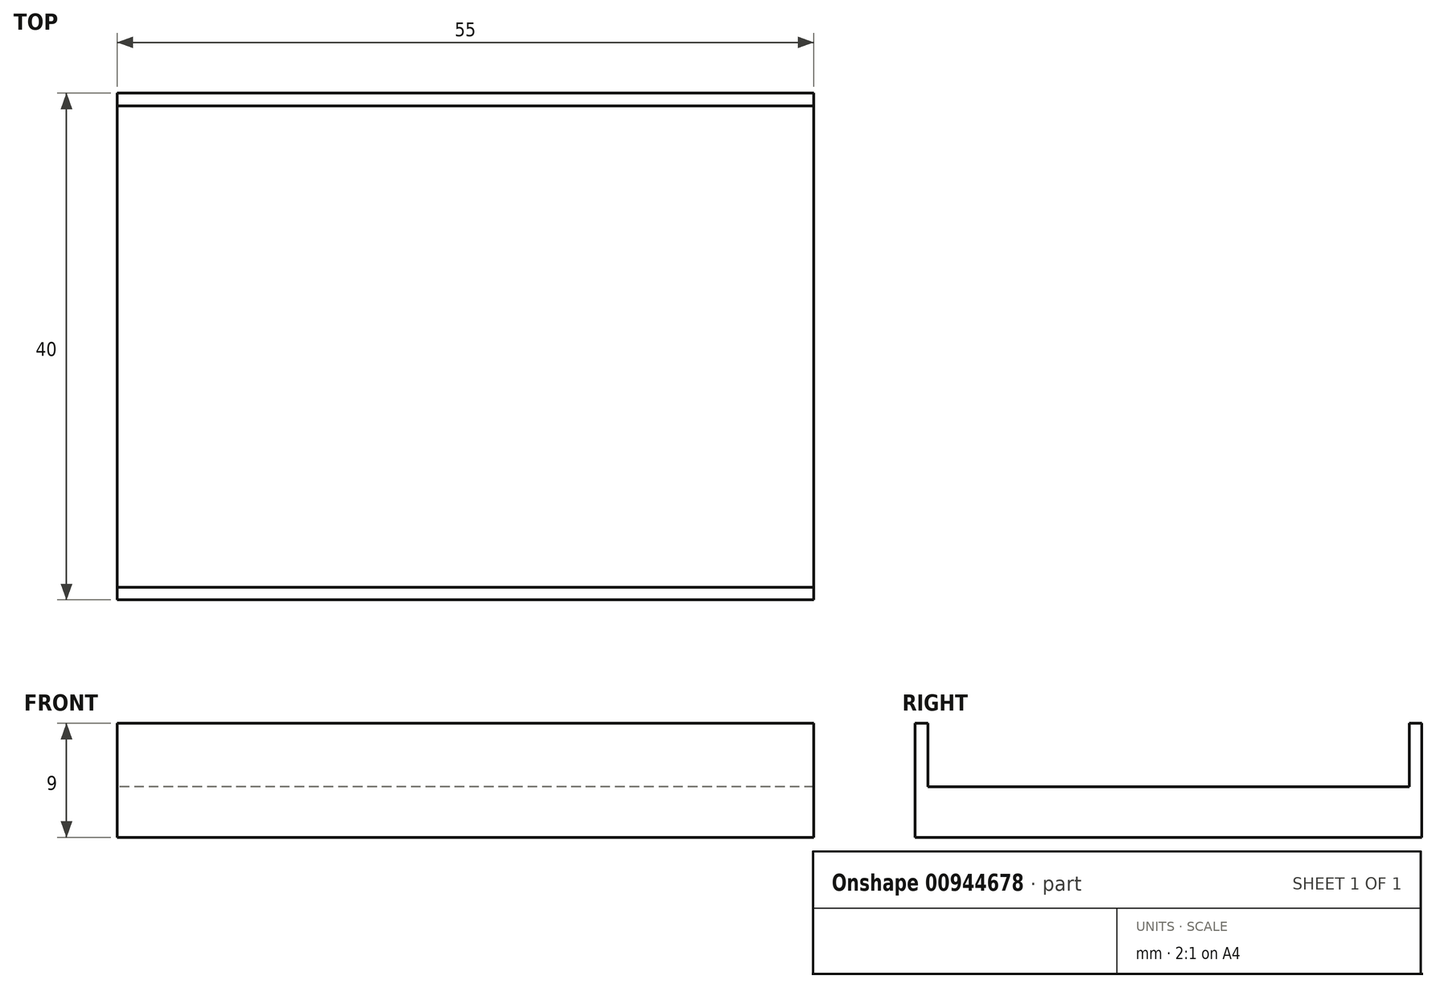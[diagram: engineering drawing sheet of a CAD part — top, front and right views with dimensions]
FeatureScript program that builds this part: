
annotation { "Feature Type Name" : "Feature", "Feature Type Description" : "" }
export const myFeature = defineFeature(function(context is Context, id is Id, definition is map)
    precondition{}
    {
        {
            var Q0;
            Q0=qCreatedBy(makeId("Top.planeOp"),FACE);
            var sketch = newSketch(context, id + "F0", { "sketchPlane" : qUnion([Q0])});
            skLineSegment(sketch, "E0.bottom", {"start": v(27.5, 20) * mm, "end": v(-27.5, 20) * mm});
            skLineSegment(sketch, "E0.top", {"start": v(27.5, -20) * mm, "end": v(-27.5, -20) * mm});
            skLineSegment(sketch, "E0.left", {"start": v(27.5, 20) * mm, "end": v(27.5, -20) * mm});
            skLineSegment(sketch, "E0.right", {"start": v(-27.5, 20) * mm, "end": v(-27.5, -20) * mm});
            skPoint(sketch, "E0.middle", {"position": v(0, 0) * mm});
            skSolve(sketch);
        }
        {
            var Q0;
            Q0=makeQuery(id+"F0.imprint","IMPRINT",FACE,{"disambiguationData":[TD([[makeQuery(id+"F0.imprint","IMPRINT",EDGE,{"derivedFrom":sQuery(id+"F0.wireOp",EDGE,"E0.bottom")}),1.0]])]});
            extrude(context, id + "F1", {"entities" : qUnion([Q0]), "depth" : 4 * mm, "offsetDistance" : 25 * mm});
        }
        {
            var Q0;
            Q0=makeQuery(id+"F1.opExtrude","CAP_FACE",FACE,{"disambiguationData":[OSD([sQuery(id+"F0.wireOp",EDGE,"E0.bottom"),sQuery(id+"F0.wireOp",EDGE,"E0.top"),sQuery(id+"F0.wireOp",EDGE,"E0.left"),sQuery(id+"F0.wireOp",EDGE,"E0.right")])],"isStart":false});
            var sketch = newSketch(context, id + "F2", { "sketchPlane" : qUnion([Q0])});
            skLineSegment(sketch, "E1", {"start": v(-27.5, -20) * mm, "end": v(-27.5, -19) * mm});
            skLineSegment(sketch, "E2", {"start": v(-27.5, -19) * mm, "end": v(27.5, -19) * mm});
            skLineSegment(sketch, "E3", {"start": v(27.5, -19) * mm, "end": v(27.5, -20) * mm});
            skLineSegment(sketch, "E4", {"start": v(27.5, -20) * mm, "end": v(-27.5, -20) * mm});
            skSolve(sketch);
        }
        {
            var Q0;
            Q0=makeQuery(id+"F2.imprint","IMPRINT",FACE,{"disambiguationData":[TD([[makeQuery(id+"F2.imprint","IMPRINT",EDGE,{"derivedFrom":sQuery(id+"F2.wireOp",EDGE,"E1")}),1.0]])]});
            extrude(context, id + "F3", {"entities" : qUnion([Q0]), "operationType" : NewBodyOperationType.ADD, "depth" : 5 * mm, "offsetDistance" : 25 * mm});
        }
        {
            var Q0;
            Q0=makeQuery(id+"F1.opExtrude","CAP_FACE",FACE,{"disambiguationData":[OSD([sQuery(id+"F0.wireOp",EDGE,"E0.bottom"),sQuery(id+"F0.wireOp",EDGE,"E0.top"),sQuery(id+"F0.wireOp",EDGE,"E0.left"),sQuery(id+"F0.wireOp",EDGE,"E0.right")])],"isStart":false});
            var sketch = newSketch(context, id + "F4", { "sketchPlane" : qUnion([Q0])});
            skLineSegment(sketch, "E5", {"start": v(-27.5, 20) * mm, "end": v(27.5, 20) * mm});
            skLineSegment(sketch, "E6", {"start": v(27.5, 20) * mm, "end": v(27.5, 19) * mm});
            skLineSegment(sketch, "E7", {"start": v(27.5, 19) * mm, "end": v(-27.5, 19) * mm});
            skLineSegment(sketch, "E8", {"start": v(-27.5, 19) * mm, "end": v(-27.5, 20) * mm});
            skSolve(sketch);
        }
        {
            var Q0;
            Q0=makeQuery(id+"F4.imprint","IMPRINT",FACE,{"disambiguationData":[TD([[makeQuery(id+"F4.imprint","IMPRINT",EDGE,{"derivedFrom":sQuery(id+"F4.wireOp",EDGE,"E5")}),1.0]])]});
            extrude(context, id + "F5", {"entities" : qUnion([Q0]), "operationType" : NewBodyOperationType.ADD, "depth" : 5 * mm, "offsetDistance" : 25 * mm});
        }
        {
            var Q0;
            Q0=makeQuery(id+"F1.opExtrude","CAP_FACE",FACE,{"disambiguationData":[OSD([sQuery(id+"F0.wireOp",EDGE,"E0.bottom"),sQuery(id+"F0.wireOp",EDGE,"E0.top"),sQuery(id+"F0.wireOp",EDGE,"E0.left"),sQuery(id+"F0.wireOp",EDGE,"E0.right")])],"isStart":false});
            var sketch = newSketch(context, id + "F6", { "sketchPlane" : qUnion([Q0])});
            skLineSegment(sketch, "E9", {"start": v(-27.5, 19) * mm, "end": v(-26.5, 19) * mm});
            skLineSegment(sketch, "E10", {"start": v(-26.5, 19) * mm, "end": v(-26.5, -19) * mm});
            skLineSegment(sketch, "E11", {"start": v(-26.5, -19) * mm, "end": v(-27.5, -19) * mm});
            skLineSegment(sketch, "E12", {"start": v(-27.5, -19) * mm, "end": v(-27.5, 19) * mm});
            skSolve(sketch);
        }
        {
            var Q0;
            Q0=sQuery(id+"F6.wireOp",EDGE,"E12");
            extrude(context, id + "F7", {"bodyType" : ToolBodyType.SURFACE, "surfaceEntities" : qUnion([Q0]), "depth" : 5 * mm, "offsetDistance" : 25 * mm});
        }
    });
